# Revit family: Tub_Filler_Trim-American_Standard-Roman-T061901_Series
name_source: partatom
category: Plumbing Fixtures
units: mm (PartAtom-declared; Revit-internal decimal feet)

## family parameters
Always vertical = No
Cut with Voids When Loaded = No
OmniClass Number = 23.45.55.17
OmniClass Title = Mixing Faucets
Part Type = Normal
Room Calculation Point = No
Round Connector Dimension = Use Diameter
Shared = Yes
Work Plane-Based = Yes

## types (3) — shared parameters
Assembly Code = D2020300
CEC Compliant = Yes
CW Connection = Yes
CWFU = 3
Cold Water Connection Diameter = 1/2"
Compliance Certifications = These products meet or exceed the following codes and standards: ASME A112.18.1, CSA B125.1
Default Elevation = 0"
Description = Roman Tub Filler with Shower
HW Connection = Yes
HWFU = 3
Handle Distance (8" to 16") = 8"
Height = 8"
Hot Water Connection Diameter = 1"
Installation Type = Deck Mounted
Length = 9 9/16"
Manufacturer = American Standard
Shower Width from Center = 10"
Tempered Water Connection = Yes
Tempered Water Connection Diameter = 1/2"
URL = https://www.americanstandard-us.com
Vent Connection = No
WFU = 4
Waste Connection = No
Width = 8"

## per-type parameters (varying)
| type | Finish | Material |
| T061901.002 | Brass-American Standard-002-Polished Chrome | Brass-American Standard-002-Polished Chrome |
| T061901.295 | Brass-American Standard-295-Brushed Nickel | Brass-American Standard-295-Brushed Nickel |
| T061901.243 | Brass-American Standard-243-Matte Black | Brass-American Standard-243-Matte Black |

note: column(s) folded — value = type name in every type: Model

## geometry (parser evidence)
native form markers: Sweep x6
no freeform markers — native parametric forms only
